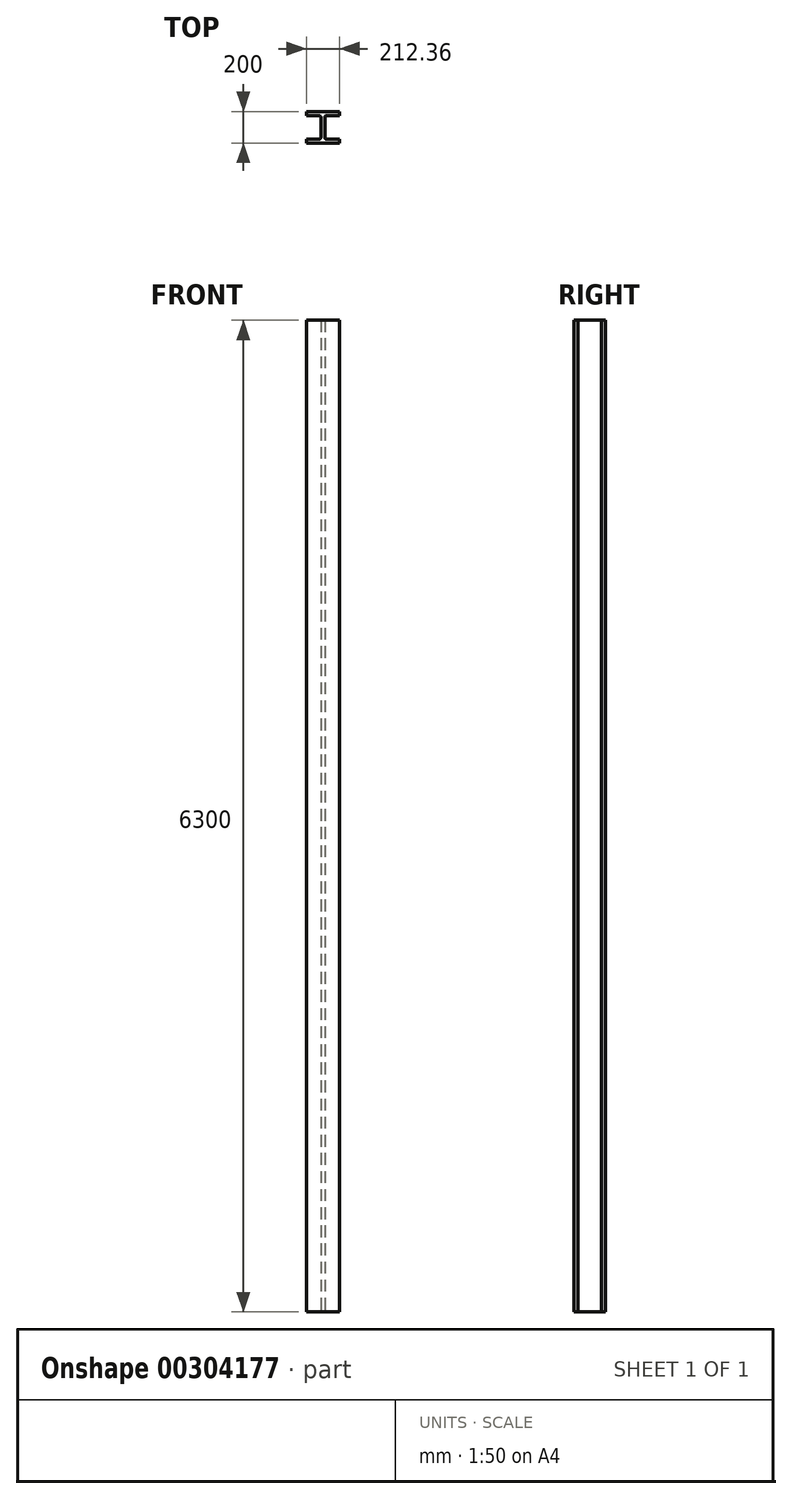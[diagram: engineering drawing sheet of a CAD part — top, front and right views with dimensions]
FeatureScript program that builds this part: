
annotation { "Feature Type Name" : "Feature", "Feature Type Description" : "" }
export const myFeature = defineFeature(function(context is Context, id is Id, definition is map)
    precondition{}
    {
        {
            var Q0;
            Q0=qCreatedBy(makeId("Top.planeOp"),FACE);
            var sketch = newSketch(context, id + "F0", { "sketchPlane" : qUnion([Q0])});
            skLineSegment(sketch, "E0", {"start": v(-123.41, 106.91) * mm, "end": v(86.59, 106.91) * mm});
            skLineSegment(sketch, "E1", {"start": v(86.59, 106.91) * mm, "end": v(86.59, 81.91) * mm});
            skLineSegment(sketch, "E2", {"start": v(86.59, 81.91) * mm, "end": v(-8.27, 81.91) * mm});
            skLineSegment(sketch, "E3", {"start": v(-8.27, 81.91) * mm, "end": v(-8.27, -68.09) * mm});
            skLineSegment(sketch, "E4", {"start": v(-8.27, -68.09) * mm, "end": v(84.23, -68.09) * mm});
            skLineSegment(sketch, "E5", {"start": v(84.23, -68.09) * mm, "end": v(84.23, -93.09) * mm});
            skLineSegment(sketch, "E6", {"start": v(84.23, -93.09) * mm, "end": v(-125.77, -93.09) * mm});
            skLineSegment(sketch, "E7", {"start": v(-125.77, -93.09) * mm, "end": v(-125.77, -68.09) * mm});
            skLineSegment(sketch, "E8", {"start": v(-125.77, -68.09) * mm, "end": v(-33.27, -68.09) * mm});
            skLineSegment(sketch, "E9", {"start": v(-33.27, -68.09) * mm, "end": v(-33.27, 81.91) * mm});
            skLineSegment(sketch, "E10", {"start": v(-33.27, 81.91) * mm, "end": v(-123.41, 81.91) * mm});
            skLineSegment(sketch, "E11", {"start": v(-123.41, 81.91) * mm, "end": v(-123.41, 106.91) * mm});
            skSolve(sketch);
        }
        {
            var Q0;
            Q0=makeQuery(id+"F0.imprint","IMPRINT",FACE,{"disambiguationData":[TD([[makeQuery(id+"F0.imprint","IMPRINT",EDGE,{"derivedFrom":sQuery(id+"F0.wireOp",EDGE,"E0")}),-1.0]])]});
            extrude(context, id + "F1", {"entities" : qUnion([Q0]), "depth" : 6300 * mm});
        }
        {
            var Q0;
            Q0=makeQuery(id+"F1.opExtrude","SWEPT_EDGE",EDGE,{"disambiguationData":[OSD([sQuery(id+"F0.wireOp",EDGE,"E2"),sQuery(id+"F0.wireOp",EDGE,"E3")])]});
            var Q1;
            Q1=makeQuery(id+"F1.opExtrude","SWEPT_EDGE",EDGE,{"disambiguationData":[OSD([sQuery(id+"F0.wireOp",EDGE,"E9"),sQuery(id+"F0.wireOp",EDGE,"E10")])]});
            var Q2;
            Q2=makeQuery(id+"F1.opExtrude","SWEPT_EDGE",EDGE,{"disambiguationData":[OSD([sQuery(id+"F0.wireOp",EDGE,"E8"),sQuery(id+"F0.wireOp",EDGE,"E9")])]});
            var Q3;
            Q3=makeQuery(id+"F1.opExtrude","SWEPT_EDGE",EDGE,{"disambiguationData":[OSD([sQuery(id+"F0.wireOp",EDGE,"E3"),sQuery(id+"F0.wireOp",EDGE,"E4")])]});
            fillet(context, id + "F2", {"entities" : qUnion([Q0, Q1, Q2, Q3]), "radius" : 10 * mm, "tangentPropagation" : true, "allowEdgeOverflow" : false});
        }
    });
